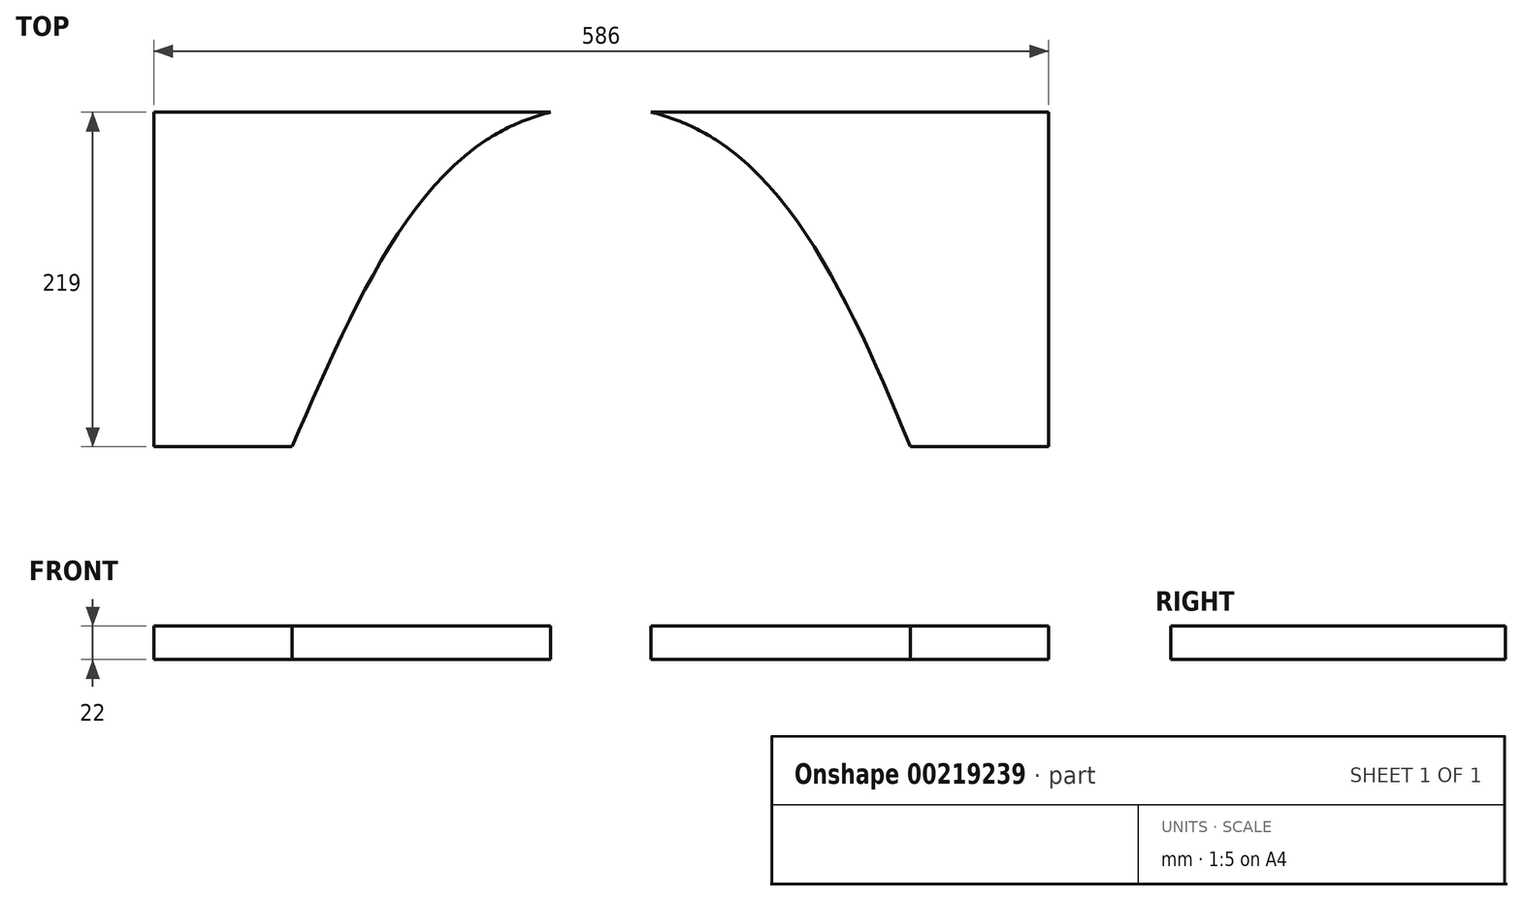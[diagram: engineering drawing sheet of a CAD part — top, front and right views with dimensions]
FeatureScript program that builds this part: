
annotation { "Feature Type Name" : "Feature", "Feature Type Description" : "" }
export const myFeature = defineFeature(function(context is Context, id is Id, definition is map)
    precondition{}
    {
        {
            var Q0;
            Q0=qCreatedBy(makeId("Top.planeOp"),FACE);
            var sketch = newSketch(context, id + "F0", { "sketchPlane" : qUnion([Q0])});
            skLineSegment(sketch, "E0.bottom", {"start": v(293, -109.5) * mm, "end": v(-293, -109.5) * mm});
            skLineSegment(sketch, "E0.top", {"start": v(293, 109.5) * mm, "end": v(-293, 109.5) * mm});
            skLineSegment(sketch, "E0.left", {"start": v(293, -109.5) * mm, "end": v(293, 109.5) * mm});
            skLineSegment(sketch, "E0.right", {"start": v(-293, -109.5) * mm, "end": v(-293, 109.5) * mm});
            skPoint(sketch, "E0.middle", {"position": v(0, 0) * mm});
            skLineSegment(sketch, "E1", {"start": v(-75, 91.5) * mm, "end": v(-11, 91.5) * mm});
            skLineSegment(sketch, "E2.top", {"start": v(-11, 100.5) * mm, "end": v(11, 100.5) * mm});
            skLineSegment(sketch, "E2.left", {"start": v(-11, 91.5) * mm, "end": v(-11, 100.5) * mm});
            skLineSegment(sketch, "E2.right", {"start": v(11, 91.5) * mm, "end": v(11, 100.5) * mm});
            skLineSegment(sketch, "E3.trimOffspring", {"start": v(11, 91.5) * mm, "end": v(74.93, 91.5) * mm});
            skPoint(sketch, "E4", {"position": v(202.5, -109.5) * mm});
            skPoint(sketch, "E5", {"position": v(-202.5, -109.5) * mm});
            skFitSpline(sketch, "E6", {"points": [v(202.5, -109.5) * mm, v(74.93, 91.5) * mm, v(-75, 91.5) * mm, v(-202.5, -109.5) * mm], "startDerivative": vector(-282.07, 680.32) * mm, "endDerivative": vector(-296.37, -676.31) * mm});
            skSolve(sketch);
        }
        {
            var Q0;
            Q0=makeQuery(id+"F0.imprint","IMPRINT",FACE,{"disambiguationData":[TD([[makeQuery(id+"F0.imprint","IMPRINT",EDGE,{"derivedFrom":sQuery(id+"F0.wireOp",EDGE,"E0.top")}),1.0]])]});
            extrude(context, id + "F1", {"entities" : qUnion([Q0]), "depth" : 22 * mm});
        }
    });
